# Revit family: BIMLIB_Адаптер_НР_РОСТерм
name_source: partatom
category: Соединительные детали трубопроводов
revit_build: Autodesk Revit 2017 (Build: 20170118_1100(x64)
units: mm (PartAtom-declared; Revit-internal decimal feet)

## family parameters
Всегда вертикально = Да
На основе рабочей плоскости = Нет
Общий = Нет
При загрузке вырезать с полостями = Нет
Размер круглого соединителя = Использовать диаметр
Тип детали = Переход

## types (1)
- Адаптер для медных трубок НР
    ADSK_URL документации изделия = http://rostherm.ru
    ADSK_URL страницы изделия = http://rostherm.ru
    ADSK_Версия Revit = 2017
    ADSK_Единица измерения = шт.
    ADSK_Завод-изготовитель = РОСТерм
    ADSK_Материал = BIMLIB_Латунь_РТ
    ADSK_Наименование = Адаптер для медных трубок НР 15х1/2''
    ADSK_Наименование краткое = Адаптер НР 15х1/2''
    ADSK_Обозначение = ГОСТ 32415-2013
    BL_BIM library = https://bimlib.pro
    URL = http://rostherm.ru
    Изготовитель = РОСТерм
    Изображение типоразмера = <Нет>
    Описание = Адаптер для медных трубок НР
    РТ_A = 19 мм
    РТ_DN = 15 мм
    РТ_L = 7 мм
    РТ_L1 = 29 мм
    РТ_Rвн = 5 мм
    РТ_Rвнеш = 10 мм

## geometry (parser evidence)
native form markers: Sweep x1
no freeform markers — native parametric forms only
